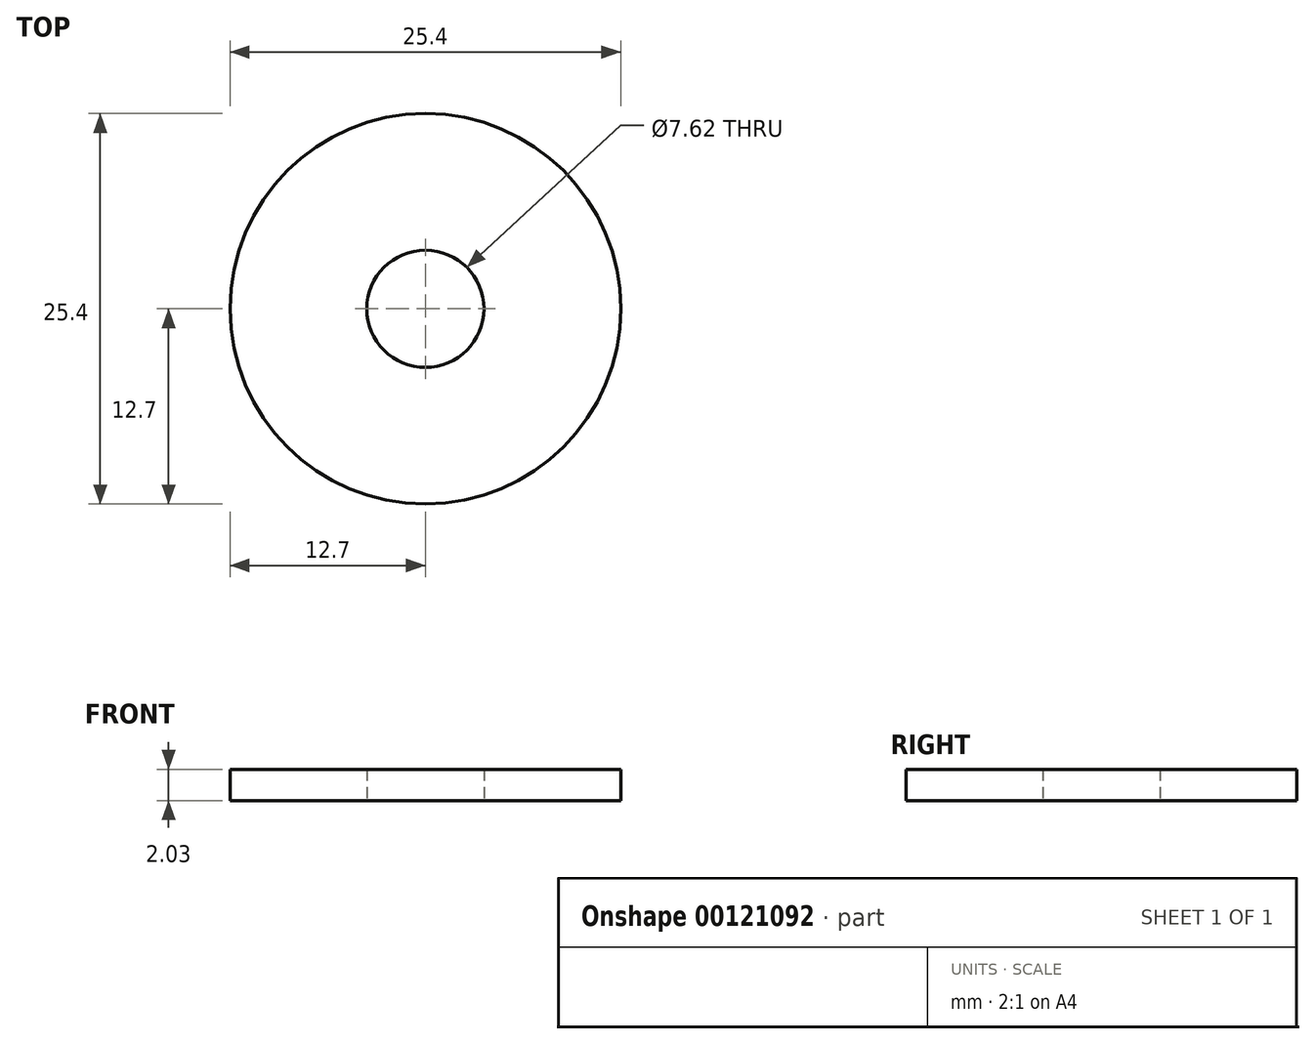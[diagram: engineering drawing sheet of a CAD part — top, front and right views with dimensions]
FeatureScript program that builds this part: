
annotation { "Feature Type Name" : "Feature", "Feature Type Description" : "" }
export const myFeature = defineFeature(function(context is Context, id is Id, definition is map)
    precondition{}
    {
        {
            var Q0;
            Q0=qCreatedBy(makeId("Top.planeOp"),FACE);
            var sketch = newSketch(context, id + "F0", { "sketchPlane" : qUnion([Q0])});
            skCircle(sketch, "E0", {"center": v(0, 0) * mm, "radius": 12.7 * mm});
            skCircle(sketch, "E1", {"center": v(0, 0) * mm, "radius": 3.81 * mm});
            skSolve(sketch);
        }
        {
            var Q0;
            Q0 = qSketchRegion(id + "F0", true);
            extrude(context, id + "F1", {"entities" : qUnion([Q0]), "depth" : 2.03 * mm});
        }
    });
